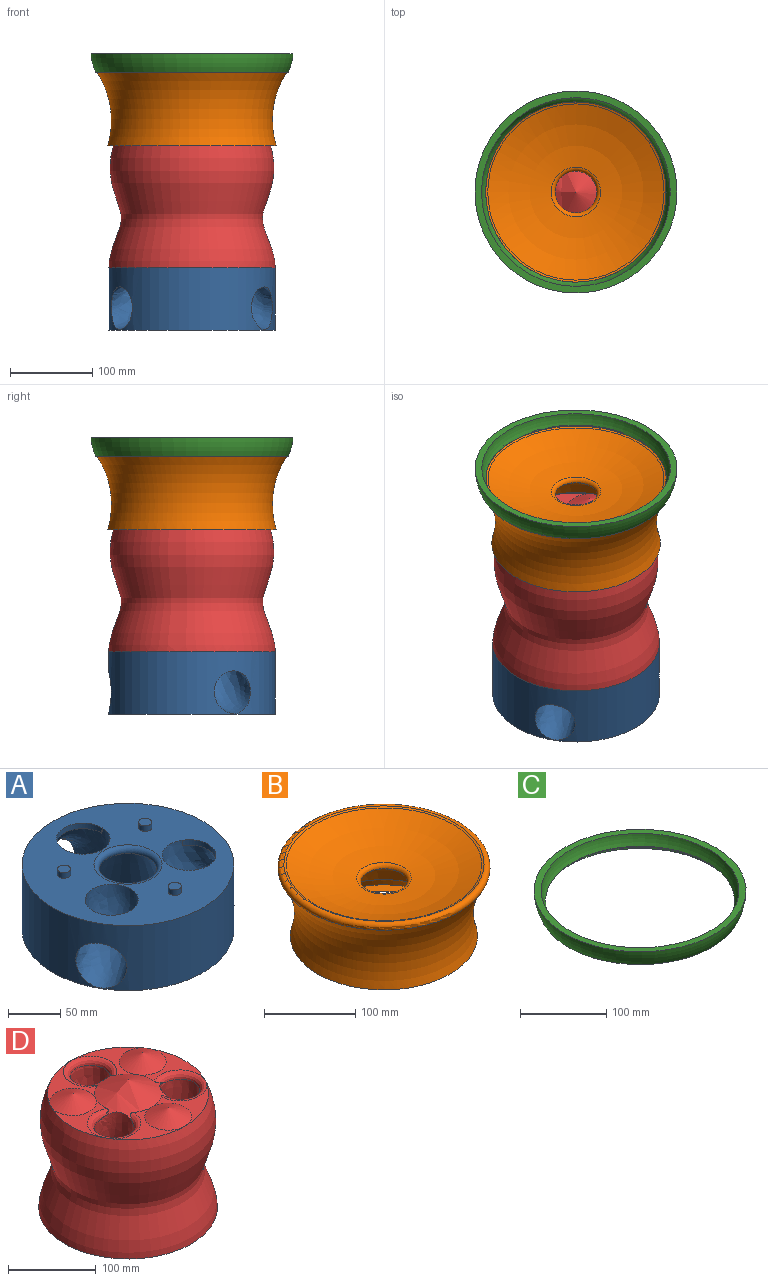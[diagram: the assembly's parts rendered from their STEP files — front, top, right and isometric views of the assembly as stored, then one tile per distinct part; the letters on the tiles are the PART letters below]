
ASSEMBLY  parts=4 mates=5
PART A: 20 faces, bbox 223.2x223.7x86.9 mm
  f0: cylinder r=101.6mm len=203.2mm, axis (0,0,-1), area 42377.7mm2, adj f1,f2,f7,f8,f9
  f1: plane 207.6x207.6mm, normal (0,0,1), area 22512.6mm2, adj f0,f3,f4,f5,f6,f7,f8,f9
  f2: plane 203.2x203.2mm, normal (0,0,-1), area 32429.3mm2, adj f0
  f3: cylinder r=25.4mm len=47.63mm, axis (0,0,1), area 509.7mm2, adj f1,f8
  f4: cylinder r=25.4mm len=47.63mm, axis (0,0,1), area 509.7mm2, adj f1,f9
  f5: cylinder r=25.4mm len=50.8mm, axis (0,0,1), area 509.7mm2, adj f1,f6,f7
  f6: bspline ~6.4x1.41mm, area 1.5mm2, adj f1,f5,f7
  f7: bspline ~82.72x78.09mm, area 10157.9mm2, adj f0,f1,f5,f6
  f8: bspline ~82.79x77.92mm, area 10164.4mm2, adj f0,f1,f3
  f9: bspline ~82.39x78.31mm, area 10158.7mm2, adj f0,f1,f4
  f10: cone r=25.4mm half-angle=20deg, axis (0,0,-1), area 14325.3mm2, adj f18,f19
  f11: plane 87.14x87.14mm, normal (0,0,1), area 5963.4mm2, adj f19
  f12: cylinder r=6.35mm len=12.7mm, axis (0,0,-1), area 253.4mm2, adj f1,f13
  f13: plane 12.7x12.7mm, normal (0,0,1), area 126.7mm2, adj f12
  f14: cylinder r=6.35mm len=12.7mm, axis (0,0,-1), area 253.4mm2, adj f1,f15
  f15: plane 12.7x12.7mm, normal (0,0,1), area 126.7mm2, adj f14
  f16: cylinder r=6.35mm len=12.7mm, axis (0,0,-1), area 253.4mm2, adj f1,f17
  f17: plane 12.7x12.7mm, normal (0,0,1), area 126.7mm2, adj f16
  f18: torus R=32.65mm, axis (0,0,1), area 1783.5mm2, adj f1,f10
  f19: torus R=43.57mm, axis (0,0,1), area 2887.4mm2, adj f10,f11
PART B: 12 faces, bbox 278.3x278.3x149.8 mm
  f0: revolved ~192.76x192.76mm, area 13556.7mm2, adj f3,f10
  f1: torus R=12.81mm, axis (0,0,1), area 34701.8mm2, adj f6,f8
  f2: cone r=12.59mm half-angle=66.6deg, axis (0,0,-1), area 14816.9mm2, adj f3,f9
  f3: torus R=10.76mm, axis (0,0,1), area 24208.7mm2, adj f0,f2
  f4: plane 205.31x205.31mm, normal (0,0,-1), area 11147.2mm2, adj f5,f11
  f5: torus R=203.45mm, axis (0,0,1), area 60046.1mm2, adj f4,f7
  f6: torus R=117.26mm, axis (0,0,-1), area 1843.9mm2, adj f1,f7
  f7: torus R=111.33mm, axis (0,0,-1), area 8959.8mm2, adj f5,f6
  f8: torus R=30.48mm, axis (0,0,1), area 1296.6mm2, adj f1,f9
  f9: torus R=29.5mm, axis (0,0,1), area 446mm2, adj f2,f8
  f10: plane 192.76x192.76mm, normal (0,0,1), area 7223.4mm2, adj f0,f11
  f11: cylinder r=83.61mm len=167.21mm, axis (0,0,-1), area 262.7mm2, adj f4,f10
PART C: 7 faces, bbox 266.5x266.5x42 mm
  f0: torus R=68.15mm, axis (0,0,1), area 17683.5mm2, adj f1,f6
  f1: plane 246.12x246.12mm, normal (0,0,1), area 6136.4mm2, adj f0,f2
  f2: torus R=74.75mm, axis (0,0,1), area 11054.5mm2, adj f1,f3
  f3: cone r=109.81mm half-angle=78.5deg, axis (0,0,1), area 1141.3mm2, adj f2,f4
  f4: torus R=111.34mm, axis (0,0,1), area 6649.8mm2, adj f3,f5
  f5: cone r=116.48mm half-angle=6.1deg, axis (0,0,1), area 1266.2mm2, adj f4,f6
  f6: plane 234.29x234.29mm, normal (0,0,-1), area 619.9mm2, adj f0,f5
PART D: 27 faces, bbox 209.6x214.6x185.3 mm
  f0: plane 89.94x58.44mm, normal (0,0,1), area 1120.7mm2, adj f1,f24,f25,f26
  f1: cone r=26.67mm half-angle=65deg, axis (0,0,-1), area 2465.6mm2, adj f0,f2
  f2: plane 158.38x72.39mm, normal (0,0,1), area 2245.5mm2, adj f1,f3,f23,f24,f26
  f3: cone r=26.67mm half-angle=65deg, axis (0,0,-1), area 2465.6mm2, adj f2,f4
  f4: plane 89.25x58.44mm, normal (0,0,1), area 1120.5mm2, adj f3,f5,f24,f26
  f5: bspline ~60.98x60.97mm, area 1530.1mm2, adj f4,f6,f20,f24,f26
  f6: bspline ~160.34x54.78mm, area 22167.9mm2, adj f5,f7,f18,f19,f26
  f7: plane 209.56x209.56mm, normal (0,0,-1), area 27043.5mm2, adj f6,f8,f10,f12,f14,f15,f16,f18
  f8: cylinder r=6.99mm len=13.97mm, axis (0,0,-1), area 334.4mm2, adj f7,f9
  f9: plane 13.97x13.97mm, normal (0,0,-1), area 153.3mm2, adj f8
  f10: cylinder r=6.99mm len=13.97mm, axis (0,0,-1), area 334.4mm2, adj f7,f11
  f11: plane 13.97x13.97mm, normal (0,0,-1), area 153.3mm2, adj f10
  f12: cylinder r=6.99mm len=13.97mm, axis (0,0,-1), area 334.4mm2, adj f7,f13
  f13: plane 13.97x13.97mm, normal (0,0,-1), area 153.3mm2, adj f12
  f14: cylinder r=22.86mm len=45.72mm, axis (0,0,1), area 0mm2, adj f7,f15
  f15: bspline ~160.28x102.2mm, area 22206.5mm2, adj f7,f14,f23,f26
  f16: bspline ~159.96x54.47mm, area 22140.9mm2, adj f7,f17,f25,f26
  f17: cylinder r=22.86mm len=8.29mm, axis (0,0,1), area 0mm2, adj f16,f26
  f18: cylinder r=22.86mm len=42.66mm, axis (0,0,1), area 13.5mm2, adj f6,f7
  f19: cylinder r=22.86mm len=5.1mm, axis (0,0,1), area 0mm2, adj f6,f26
  f20: plane 77.91x60.61mm, normal (0,0,1), area 1120.5mm2, adj f5,f21,f24,f26
  f21: cone r=26.67mm half-angle=65deg, axis (0,0,-1), area 2465.6mm2, adj f20,f22
  f22: plane 78.32x60.57mm, normal (0,0,1), area 1120.8mm2, adj f21,f24,f25,f26
  f23: bspline ~60.98x58.36mm, area 1524.2mm2, adj f2,f15,f26
  f24: revolved ~203.2x203.2mm, area 195469.6mm2, adj f0,f2,f4,f5,f7,f20,f22,f25
  f25: bspline ~61x60.98mm, area 1522.1mm2, adj f0,f16,f22,f24,f26
  f26: cone r=0mm half-angle=63.4deg, axis (0,0,-1), area 5350mm2, adj f0,f2,f4,f5,f6,f15,f16,f17
PLACE A t=(23.92,-129.91,-225.98)mm
PLACE B t=(69.78,-129.91,-53.67)mm
PLACE C t=(69.78,-129.91,-53.56)mm
PLACE D t=(23.92,-129.91,28.02)mm
MATE cylindrical D.f12 <-> A.f14  axis (0,0,-1) through (23.92,-193.41,-149.78)mm
MATE cylindrical A.f0 <-> D.f26  axis (0,0,-1) through (23.92,-129.91,-225.98)mm
MATE planar A.f10 <-> D.f7  axis (0,0,1) through (23.92,-129.91,-149.78)mm
MATE cylindrical C.f0 <-> A.f0  axis (0,0,-1) through (23.92,-129.91,88.19)mm
MATE cylindrical B.f1 <-> A.f0  axis (0,0,-1) through (23.92,-129.91,-1.27)mm
